# Revit family: RN 90079 Optifitt-Serra-Nippel doppio ridotto
name_source: partatom
category: Rohrformteile
units: mm (PartAtom-declared; Revit-internal decimal feet)

## family parameters
Arbeitsebenenbasiert = Nein
Beim Laden mit Abzugskörper schneiden = Nein
Bemaßung runder Anschluss = Durchmesser verwenden
Gemeinsam genutzt = Nein
Immer vertikal = Ja
Teiletyp = Nicht definiert

## types (11) — shared parameters
1.010.00.2 Blattnummer der Richtlinie = 29
1.010.00.3 Ausgabedatum (Monat) der Richtlinie = 201308
1.010.00.4 Herstellername = R. Nussbaum AG
1.010.00.5 Revisionsdatum der Datei = 20190521
1.010.00.6 Webadresse des Herstellers = http://www.nussbaum.ch
1.100.00.4 Produktbezeichnung = Versorgung
1.110.00.2 Index = 3
1.110.00.4 Produktbezeichnung = Optifitt-Serra
1.960/3L.00.8 Link (URL) = https://www.nussbaum.ch
29.700.00.4 Produktname = Optifitt-Serra-Doppelnippel reduziert
29.700.00.5 Produktkennung = 2
29.700.00.6 Querschnittsform = 1
29.700.00.7 Nennweitensystem = DN
29.700.00.8 Nenndrucksystem = PN
29.710.02.4 Nenndruck = 16
29.710.02.5 max. zul. Überdruck [hPa] = 1600
29.710.02.7 max. zul. Dauer-Betriebsdruck [hPa] = 1600
29.710.02.9 max. zul. Dauer-Betriebstemperatur [°C] = 90
Connector Visibility = Nein
EnclosingSpace Visibility = Nein
Hersteller = R. Nussbaum AG
URL = https://www.nussbaum.ch

## per-type parameters (varying)
- DN=50x40: 1.800.00.3 TGA-Nummer=01900300000000000000000000000000000000000000000016000000000000000024; 1.800.00.4 Kommentarfeld=90079.35, Optifitt-Serra-Doppelnippel reduziert, DN=50x40, L=64, R=2; 1.810.00.3 Hersteller-Bestellnummer=90079.35; 1.810.00.4 DATANORM-Nummer=90079.35; 1.810.00.5 StLB-Nummer=214.557; 1.810.00.6 GTIN-Nummer=7612945680440; 29.710.02.10 Formstück-Gewicht [kg]=0.436; 29.710.02.3 Benennung=Optifitt-Serra-Doppelnippel reduziert, DN=50x40, L=64, R=2; CONNECTOR0_DIAMETER_dX_0r=50 mm; CONNECTOR0_dX_01=24 mm; CONNECTOR0_ref_dX=24 mm; CONNECTOR1_DIAMETER_dX_0r=40 mm  [stored 0.131234 ft]; CONNECTOR1_dX_00=45 mm  [stored 0.147638 ft]; CONNECTOR1_dX_01=64 mm; CONNECTOR1_ref_dX=45 mm  [stored 0.147638 ft]; CONNECTOR1_ref_dX2=64 mm; Modell=90079.35; R. Nussbaum AG 90079.22 de Visibility=Nein; R. Nussbaum AG 90079.24 de Visibility=Nein; R. Nussbaum AG 90079.25 de Visibility=Nein; R. Nussbaum AG 90079.26 de Visibility=Nein; R. Nussbaum AG 90079.27 de Visibility=Nein; R. Nussbaum AG 90079.28 de Visibility=Nein; R. Nussbaum AG 90079.29 de Visibility=Nein; R. Nussbaum AG 90079.31 de Visibility=Nein; R. Nussbaum AG 90079.32 de Visibility=Nein; R. Nussbaum AG 90079.34 de Visibility=Nein; R. Nussbaum AG 90079.35 de Visibility=Ja; Typenkommentare=Optifitt-Serra-Nippel doppio ridotto  DN=50x40
- DN=50x32: 1.800.00.3 TGA-Nummer=01900300000000000000000000000000000000000000000016000000000000000023; 1.800.00.4 Kommentarfeld=90079.34, Optifitt-Serra-Doppelnippel reduziert, DN=50x32, L=58, R=2; 1.810.00.3 Hersteller-Bestellnummer=90079.34; 1.810.00.4 DATANORM-Nummer=90079.34; 1.810.00.5 StLB-Nummer=214.557; 1.810.00.6 GTIN-Nummer=7612945680433; 29.710.02.10 Formstück-Gewicht [kg]=0.394; 29.710.02.3 Benennung=Optifitt-Serra-Doppelnippel reduziert, DN=50x32, L=58, R=2; CONNECTOR0_DIAMETER_dX_0r=50 mm; CONNECTOR0_dX_01=24 mm; CONNECTOR0_ref_dX=24 mm; CONNECTOR1_DIAMETER_dX_0r=32 mm  [stored 0.104987 ft]; CONNECTOR1_dX_00=39 mm; CONNECTOR1_dX_01=58 mm; CONNECTOR1_ref_dX=39 mm; CONNECTOR1_ref_dX2=58 mm; Modell=90079.34; R. Nussbaum AG 90079.22 de Visibility=Nein; R. Nussbaum AG 90079.24 de Visibility=Nein; R. Nussbaum AG 90079.25 de Visibility=Nein; R. Nussbaum AG 90079.26 de Visibility=Nein; R. Nussbaum AG 90079.27 de Visibility=Nein; R. Nussbaum AG 90079.28 de Visibility=Nein; R. Nussbaum AG 90079.29 de Visibility=Nein; R. Nussbaum AG 90079.31 de Visibility=Nein; R. Nussbaum AG 90079.32 de Visibility=Nein; R. Nussbaum AG 90079.34 de Visibility=Ja; R. Nussbaum AG 90079.35 de Visibility=Nein; Typenkommentare=Optifitt-Serra-Nippel doppio ridotto  DN=50x32
- DN=40x32: 1.800.00.3 TGA-Nummer=01900300000000000000000000000000000000000000000016000000000000000022; 1.800.00.4 Kommentarfeld=90079.32, Optifitt-Serra-Doppelnippel reduziert, DN=40x32, L=59, R=1½; 1.810.00.3 Hersteller-Bestellnummer=90079.32; 1.810.00.4 DATANORM-Nummer=90079.32; 1.810.00.5 StLB-Nummer=214.556; 1.810.00.6 GTIN-Nummer=7612945680426; 29.710.02.10 Formstück-Gewicht [kg]=0.307; 29.710.02.3 Benennung=Optifitt-Serra-Doppelnippel reduziert, DN=40x32, L=59, R=1½; CONNECTOR0_DIAMETER_dX_0r=40 mm  [stored 0.131234 ft]; CONNECTOR0_dX_01=19 mm; CONNECTOR0_ref_dX=19 mm; CONNECTOR1_DIAMETER_dX_0r=32 mm  [stored 0.104987 ft]; CONNECTOR1_dX_00=40 mm  [stored 0.131234 ft]; CONNECTOR1_dX_01=59 mm; CONNECTOR1_ref_dX=40 mm  [stored 0.131234 ft]; CONNECTOR1_ref_dX2=59 mm; Modell=90079.32; R. Nussbaum AG 90079.22 de Visibility=Nein; R. Nussbaum AG 90079.24 de Visibility=Nein; R. Nussbaum AG 90079.25 de Visibility=Nein; R. Nussbaum AG 90079.26 de Visibility=Nein; R. Nussbaum AG 90079.27 de Visibility=Nein; R. Nussbaum AG 90079.28 de Visibility=Nein; R. Nussbaum AG 90079.29 de Visibility=Nein; R. Nussbaum AG 90079.31 de Visibility=Nein; R. Nussbaum AG 90079.32 de Visibility=Ja; R. Nussbaum AG 90079.34 de Visibility=Nein; R. Nussbaum AG 90079.35 de Visibility=Nein; Typenkommentare=Optifitt-Serra-Nippel doppio ridotto  DN=40x32
- DN=40x25: 1.800.00.3 TGA-Nummer=01900300000000000000000000000000000000000000000016000000000000000021; 1.800.00.4 Kommentarfeld=90079.31, Optifitt-Serra-Doppelnippel reduziert, DN=40x25, L=53, R=1½; 1.810.00.3 Hersteller-Bestellnummer=90079.31; 1.810.00.4 DATANORM-Nummer=90079.31; 1.810.00.5 StLB-Nummer=214.556; 1.810.00.6 GTIN-Nummer=7612945680419; 29.710.02.10 Formstück-Gewicht [kg]=0.235; 29.710.02.3 Benennung=Optifitt-Serra-Doppelnippel reduziert, DN=40x25, L=53, R=1½; CONNECTOR0_DIAMETER_dX_0r=40 mm  [stored 0.131234 ft]; CONNECTOR0_dX_01=19 mm; CONNECTOR0_ref_dX=19 mm; CONNECTOR1_DIAMETER_dX_0r=25 mm  [stored 0.082021 ft]; CONNECTOR1_dX_00=36 mm; CONNECTOR1_dX_01=53 mm; CONNECTOR1_ref_dX=36 mm; CONNECTOR1_ref_dX2=53 mm; Modell=90079.31; R. Nussbaum AG 90079.22 de Visibility=Nein; R. Nussbaum AG 90079.24 de Visibility=Nein; R. Nussbaum AG 90079.25 de Visibility=Nein; R. Nussbaum AG 90079.26 de Visibility=Nein; R. Nussbaum AG 90079.27 de Visibility=Nein; R. Nussbaum AG 90079.28 de Visibility=Nein; R. Nussbaum AG 90079.29 de Visibility=Nein; R. Nussbaum AG 90079.31 de Visibility=Ja; R. Nussbaum AG 90079.32 de Visibility=Nein; R. Nussbaum AG 90079.34 de Visibility=Nein; R. Nussbaum AG 90079.35 de Visibility=Nein; Typenkommentare=Optifitt-Serra-Nippel doppio ridotto  DN=40x25
- DN=32x25: 1.800.00.3 TGA-Nummer=01900300000000000000000000000000000000000000000016000000000000000020; 1.800.00.4 Kommentarfeld=90079.29, Optifitt-Serra-Doppelnippel reduziert, DN=32x25, L=54, R=1¼; 1.810.00.3 Hersteller-Bestellnummer=90079.29; 1.810.00.4 DATANORM-Nummer=90079.29; 1.810.00.5 StLB-Nummer=214.555; 1.810.00.6 GTIN-Nummer=7612945680402; 29.710.02.10 Formstück-Gewicht [kg]=0.226; 29.710.02.3 Benennung=Optifitt-Serra-Doppelnippel reduziert, DN=32x25, L=54, R=1¼; CONNECTOR0_DIAMETER_dX_0r=32 mm  [stored 0.104987 ft]; CONNECTOR0_dX_01=19 mm; CONNECTOR0_ref_dX=19 mm; CONNECTOR1_DIAMETER_dX_0r=25 mm  [stored 0.082021 ft]; CONNECTOR1_dX_00=37 mm; CONNECTOR1_dX_01=54 mm; CONNECTOR1_ref_dX=37 mm; CONNECTOR1_ref_dX2=54 mm; Modell=90079.29; R. Nussbaum AG 90079.22 de Visibility=Nein; R. Nussbaum AG 90079.24 de Visibility=Nein; R. Nussbaum AG 90079.25 de Visibility=Nein; R. Nussbaum AG 90079.26 de Visibility=Nein; R. Nussbaum AG 90079.27 de Visibility=Nein; R. Nussbaum AG 90079.28 de Visibility=Nein; R. Nussbaum AG 90079.29 de Visibility=Ja; R. Nussbaum AG 90079.31 de Visibility=Nein; R. Nussbaum AG 90079.32 de Visibility=Nein; R. Nussbaum AG 90079.34 de Visibility=Nein; R. Nussbaum AG 90079.35 de Visibility=Nein; Typenkommentare=Optifitt-Serra-Nippel doppio ridotto  DN=32x25
- DN=32x20: 1.800.00.3 TGA-Nummer=01900300000000000000000000000000000000000000000016000000000000000019; 1.800.00.4 Kommentarfeld=90079.28, Optifitt-Serra-Doppelnippel reduziert, DN=32x20, L=52, R=1¼; 1.810.00.3 Hersteller-Bestellnummer=90079.28; 1.810.00.4 DATANORM-Nummer=90079.28; 1.810.00.5 StLB-Nummer=214.555; 1.810.00.6 GTIN-Nummer=7612945680396; 29.710.02.10 Formstück-Gewicht [kg]=0.206; 29.710.02.3 Benennung=Optifitt-Serra-Doppelnippel reduziert, DN=32x20, L=52, R=1¼; CONNECTOR0_DIAMETER_dX_0r=32 mm  [stored 0.104987 ft]; CONNECTOR0_dX_01=19 mm; CONNECTOR0_ref_dX=19 mm; CONNECTOR1_DIAMETER_dX_0r=20 mm; CONNECTOR1_dX_00=37 mm; CONNECTOR1_dX_01=52 mm; CONNECTOR1_ref_dX=37 mm; CONNECTOR1_ref_dX2=52 mm; Modell=90079.28; R. Nussbaum AG 90079.22 de Visibility=Nein; R. Nussbaum AG 90079.24 de Visibility=Nein; R. Nussbaum AG 90079.25 de Visibility=Nein; R. Nussbaum AG 90079.26 de Visibility=Nein; R. Nussbaum AG 90079.27 de Visibility=Nein; R. Nussbaum AG 90079.28 de Visibility=Ja; R. Nussbaum AG 90079.29 de Visibility=Nein; R. Nussbaum AG 90079.31 de Visibility=Nein; R. Nussbaum AG 90079.32 de Visibility=Nein; R. Nussbaum AG 90079.34 de Visibility=Nein; R. Nussbaum AG 90079.35 de Visibility=Nein; Typenkommentare=Optifitt-Serra-Nippel doppio ridotto  DN=32x20
- DN=32x15: 1.800.00.3 TGA-Nummer=01900300000000000000000000000000000000000000000016000000000000000018; 1.800.00.4 Kommentarfeld=90079.27, Optifitt-Serra-Doppelnippel reduziert, DN=32x15, L=48, R=1¼; 1.810.00.3 Hersteller-Bestellnummer=90079.27; 1.810.00.4 DATANORM-Nummer=90079.27; 1.810.00.5 StLB-Nummer=214.555; 1.810.00.6 GTIN-Nummer=7612945680389; 29.710.02.10 Formstück-Gewicht [kg]=0.203; 29.710.02.3 Benennung=Optifitt-Serra-Doppelnippel reduziert, DN=32x15, L=48, R=1¼; CONNECTOR0_DIAMETER_dX_0r=32 mm  [stored 0.104987 ft]; CONNECTOR0_dX_01=19 mm; CONNECTOR0_ref_dX=19 mm; CONNECTOR1_DIAMETER_dX_0r=15 mm; CONNECTOR1_dX_00=35 mm; CONNECTOR1_dX_01=48 mm; CONNECTOR1_ref_dX=35 mm; CONNECTOR1_ref_dX2=48 mm; Modell=90079.27; R. Nussbaum AG 90079.22 de Visibility=Nein; R. Nussbaum AG 90079.24 de Visibility=Nein; R. Nussbaum AG 90079.25 de Visibility=Nein; R. Nussbaum AG 90079.26 de Visibility=Nein; R. Nussbaum AG 90079.27 de Visibility=Ja; R. Nussbaum AG 90079.28 de Visibility=Nein; R. Nussbaum AG 90079.29 de Visibility=Nein; R. Nussbaum AG 90079.31 de Visibility=Nein; R. Nussbaum AG 90079.32 de Visibility=Nein; R. Nussbaum AG 90079.34 de Visibility=Nein; R. Nussbaum AG 90079.35 de Visibility=Nein; Typenkommentare=Optifitt-Serra-Nippel doppio ridotto  DN=32x15
- DN=25x20: 1.800.00.3 TGA-Nummer=01900300000000000000000000000000000000000000000016000000000000000017; 1.800.00.4 Kommentarfeld=90079.26, Optifitt-Serra-Doppelnippel reduziert, DN=25x20, L=50, R=1; 1.810.00.3 Hersteller-Bestellnummer=90079.26; 1.810.00.4 DATANORM-Nummer=90079.26; 1.810.00.5 StLB-Nummer=214.554; 1.810.00.6 GTIN-Nummer=7612945680372; 29.710.02.10 Formstück-Gewicht [kg]=0.15; 29.710.02.3 Benennung=Optifitt-Serra-Doppelnippel reduziert, DN=25x20, L=50, R=1; CONNECTOR0_DIAMETER_dX_0r=25 mm  [stored 0.082021 ft]; CONNECTOR0_dX_01=17 mm; CONNECTOR0_ref_dX=17 mm; CONNECTOR1_DIAMETER_dX_0r=20 mm; CONNECTOR1_dX_00=35 mm; CONNECTOR1_dX_01=50 mm; CONNECTOR1_ref_dX=35 mm; CONNECTOR1_ref_dX2=50 mm; Modell=90079.26; R. Nussbaum AG 90079.22 de Visibility=Nein; R. Nussbaum AG 90079.24 de Visibility=Nein; R. Nussbaum AG 90079.25 de Visibility=Nein; R. Nussbaum AG 90079.26 de Visibility=Ja; R. Nussbaum AG 90079.27 de Visibility=Nein; R. Nussbaum AG 90079.28 de Visibility=Nein; R. Nussbaum AG 90079.29 de Visibility=Nein; R. Nussbaum AG 90079.31 de Visibility=Nein; R. Nussbaum AG 90079.32 de Visibility=Nein; R. Nussbaum AG 90079.34 de Visibility=Nein; R. Nussbaum AG 90079.35 de Visibility=Nein; Typenkommentare=Optifitt-Serra-Nippel doppio ridotto  DN=25x20
- DN=25x15: 1.800.00.3 TGA-Nummer=01900300000000000000000000000000000000000000000016000000000000000016; 1.800.00.4 Kommentarfeld=90079.25, Optifitt-Serra-Doppelnippel reduziert, DN=25x15, L=43, R=1; 1.810.00.3 Hersteller-Bestellnummer=90079.25; 1.810.00.4 DATANORM-Nummer=90079.25; 1.810.00.5 StLB-Nummer=214.554; 1.810.00.6 GTIN-Nummer=7612945680365; 29.710.02.10 Formstück-Gewicht [kg]=0.119; 29.710.02.3 Benennung=Optifitt-Serra-Doppelnippel reduziert, DN=25x15, L=43, R=1; CONNECTOR0_DIAMETER_dX_0r=25 mm  [stored 0.082021 ft]; CONNECTOR0_dX_01=17 mm; CONNECTOR0_ref_dX=17 mm; CONNECTOR1_DIAMETER_dX_0r=15 mm; CONNECTOR1_dX_00=30 mm  [stored 0.0984252 ft]; CONNECTOR1_dX_01=43 mm  [stored 0.141076 ft]; CONNECTOR1_ref_dX=30 mm  [stored 0.0984252 ft]; CONNECTOR1_ref_dX2=43 mm  [stored 0.141076 ft]; Modell=90079.25; R. Nussbaum AG 90079.22 de Visibility=Nein; R. Nussbaum AG 90079.24 de Visibility=Nein; R. Nussbaum AG 90079.25 de Visibility=Ja; R. Nussbaum AG 90079.26 de Visibility=Nein; R. Nussbaum AG 90079.27 de Visibility=Nein; R. Nussbaum AG 90079.28 de Visibility=Nein; R. Nussbaum AG 90079.29 de Visibility=Nein; R. Nussbaum AG 90079.31 de Visibility=Nein; R. Nussbaum AG 90079.32 de Visibility=Nein; R. Nussbaum AG 90079.34 de Visibility=Nein; R. Nussbaum AG 90079.35 de Visibility=Nein; Typenkommentare=Optifitt-Serra-Nippel doppio ridotto  DN=25x15
- DN=20x15: 1.800.00.3 TGA-Nummer=01900300000000000000000000000000000000000000000016000000000000000015; 1.800.00.4 Kommentarfeld=90079.24, Optifitt-Serra-Doppelnippel reduziert, DN=20x15, L=45, R=¾; 1.810.00.3 Hersteller-Bestellnummer=90079.24; 1.810.00.4 DATANORM-Nummer=90079.24; 1.810.00.5 StLB-Nummer=214.553; 1.810.00.6 GTIN-Nummer=7612945680358; 29.710.02.10 Formstück-Gewicht [kg]=0.1; 29.710.02.3 Benennung=Optifitt-Serra-Doppelnippel reduziert, DN=20x15, L=45, R=¾; CONNECTOR0_DIAMETER_dX_0r=20 mm; CONNECTOR0_dX_01=15 mm; CONNECTOR0_ref_dX=15 mm; CONNECTOR1_DIAMETER_dX_0r=15 mm; CONNECTOR1_dX_00=32 mm  [stored 0.104987 ft]; CONNECTOR1_dX_01=45 mm  [stored 0.147638 ft]; CONNECTOR1_ref_dX=32 mm  [stored 0.104987 ft]; CONNECTOR1_ref_dX2=45 mm  [stored 0.147638 ft]; Modell=90079.24; R. Nussbaum AG 90079.22 de Visibility=Nein; R. Nussbaum AG 90079.24 de Visibility=Ja; R. Nussbaum AG 90079.25 de Visibility=Nein; R. Nussbaum AG 90079.26 de Visibility=Nein; R. Nussbaum AG 90079.27 de Visibility=Nein; R. Nussbaum AG 90079.28 de Visibility=Nein; R. Nussbaum AG 90079.29 de Visibility=Nein; R. Nussbaum AG 90079.31 de Visibility=Nein; R. Nussbaum AG 90079.32 de Visibility=Nein; R. Nussbaum AG 90079.34 de Visibility=Nein; R. Nussbaum AG 90079.35 de Visibility=Nein; Typenkommentare=Optifitt-Serra-Nippel doppio ridotto  DN=20x15
- DN=15x12: 1.800.00.3 TGA-Nummer=01900300000000000000000000000000000000000000000016000000000000000014; 1.800.00.4 Kommentarfeld=90079.22, Optifitt-Serra-Doppelnippel reduziert, DN=15x12, L=41, R=½; 1.810.00.3 Hersteller-Bestellnummer=90079.22; 1.810.00.4 DATANORM-Nummer=90079.22; 1.810.00.5 StLB-Nummer=214.552; 1.810.00.6 GTIN-Nummer=7612945680341; 29.710.02.10 Formstück-Gewicht [kg]=0.07; 29.710.02.3 Benennung=Optifitt-Serra-Doppelnippel reduziert, DN=15x12, L=41, R=½; CONNECTOR0_DIAMETER_dX_0r=15 mm; CONNECTOR0_dX_01=13 mm  [stored 0.0426509 ft]; CONNECTOR0_ref_dX=13 mm  [stored 0.0426509 ft]; CONNECTOR1_DIAMETER_dX_0r=10 mm  [stored 0.0328084 ft]; CONNECTOR1_dX_00=31 mm; CONNECTOR1_dX_01=41 mm; CONNECTOR1_ref_dX=31 mm; CONNECTOR1_ref_dX2=41 mm; Modell=90079.22; R. Nussbaum AG 90079.22 de Visibility=Ja; R. Nussbaum AG 90079.24 de Visibility=Nein; R. Nussbaum AG 90079.25 de Visibility=Nein; R. Nussbaum AG 90079.26 de Visibility=Nein; R. Nussbaum AG 90079.27 de Visibility=Nein; R. Nussbaum AG 90079.28 de Visibility=Nein; R. Nussbaum AG 90079.29 de Visibility=Nein; R. Nussbaum AG 90079.31 de Visibility=Nein; R. Nussbaum AG 90079.32 de Visibility=Nein; R. Nussbaum AG 90079.34 de Visibility=Nein; R. Nussbaum AG 90079.35 de Visibility=Nein; Typenkommentare=Optifitt-Serra-Nippel doppio ridotto  DN=15x12

note: [stored X ft] marks values corroborated as IEEE doubles in the binary element streams (Revit-internal decimal feet)

## geometry (parser evidence)
native form markers: Sweep x1
no freeform markers — native parametric forms only
